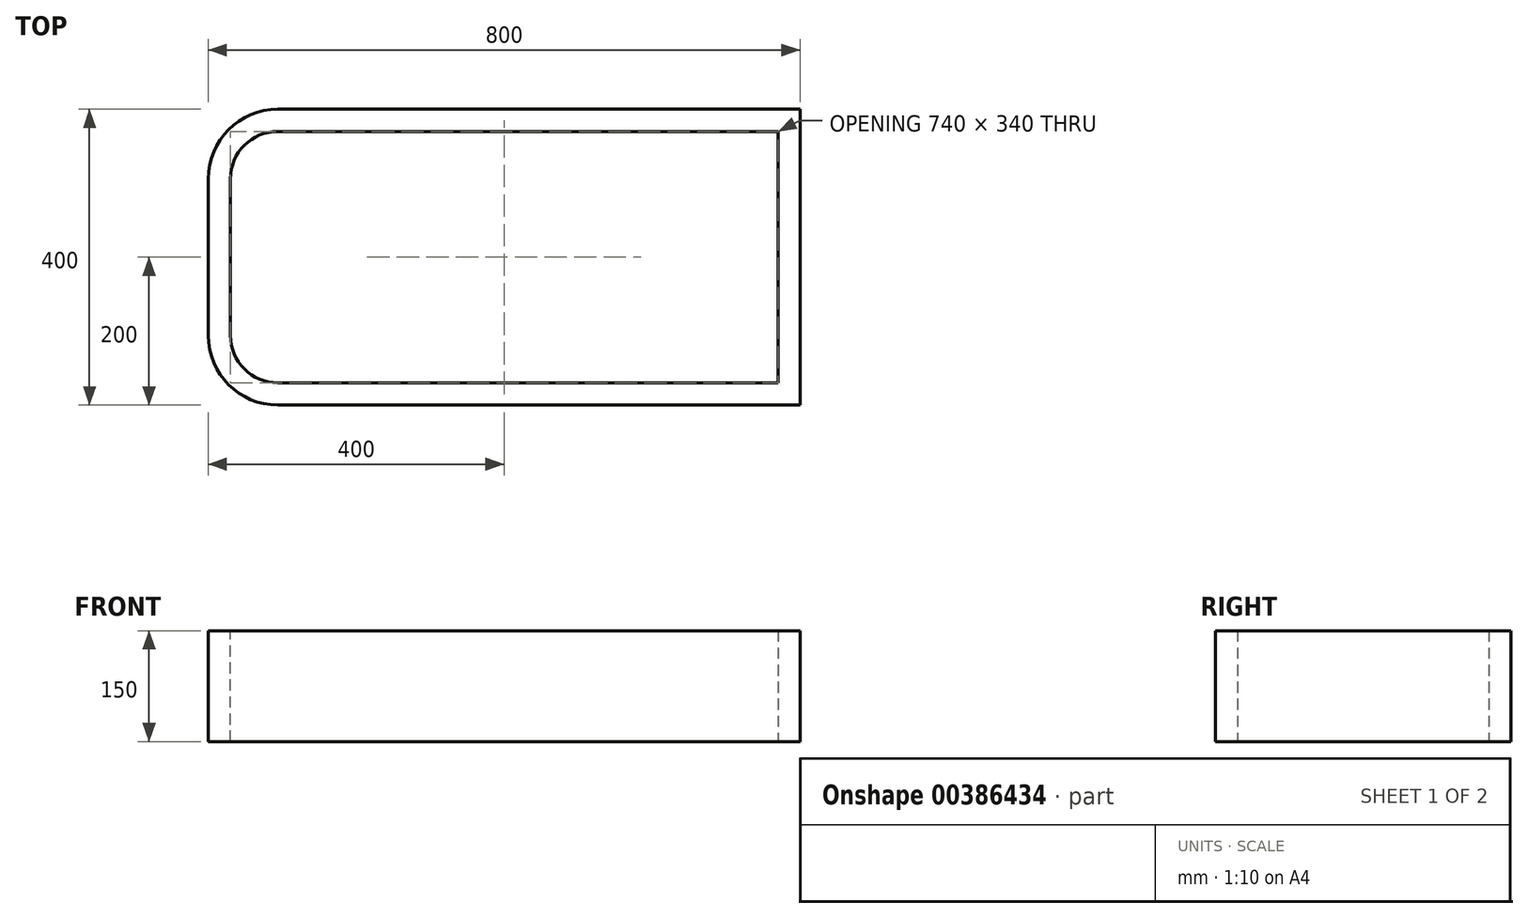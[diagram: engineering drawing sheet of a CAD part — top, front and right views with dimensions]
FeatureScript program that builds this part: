
annotation { "Feature Type Name" : "Feature", "Feature Type Description" : "" }
export const myFeature = defineFeature(function(context is Context, id is Id, definition is map)
    precondition{}
    {
        {
            var Q0;
            Q0=qCreatedBy(makeId("Top.planeOp"),FACE);
            var sketch = newSketch(context, id + "F0", { "sketchPlane" : qUnion([Q0])});
            skLineSegment(sketch, "E0.bottom", {"start": v(400, -200) * mm, "end": v(-400, -200) * mm});
            skLineSegment(sketch, "E0.top", {"start": v(400, 200) * mm, "end": v(-400, 200) * mm});
            skLineSegment(sketch, "E0.left", {"start": v(400, -200) * mm, "end": v(400, 200) * mm});
            skLineSegment(sketch, "E0.right", {"start": v(-400, -200) * mm, "end": v(-400, 200) * mm});
            skPoint(sketch, "E0.middle", {"position": v(0, 0) * mm});
            skSolve(sketch);
        }
        {
            var Q0;
            Q0=makeQuery(id+"F0.imprint","IMPRINT",FACE,{"disambiguationData":[TD([[makeQuery(id+"F0.imprint","IMPRINT",EDGE,{"derivedFrom":sQuery(id+"F0.wireOp",EDGE,"E0.bottom")}),-1.0]])]});
            extrude(context, id + "F1", {"entities" : qUnion([Q0]), "depth" : 150 * mm});
        }
        {
            var Q0;
            Q0=makeQuery(id+"F1.opExtrude","SWEPT_EDGE",EDGE,{"disambiguationData":[OSD([sQuery(id+"F0.wireOp",EDGE,"E0.top"),sQuery(id+"F0.wireOp",EDGE,"E0.right")])]});
            var Q1;
            Q1=makeQuery(id+"F1.opExtrude","SWEPT_EDGE",EDGE,{"disambiguationData":[OSD([sQuery(id+"F0.wireOp",EDGE,"E0.bottom"),sQuery(id+"F0.wireOp",EDGE,"E0.right")])]});
            fillet(context, id + "F2", {"entities" : qUnion([Q0, Q1]), "radius" : 94.15 * mm, "tangentPropagation" : true, "allowEdgeOverflow" : false});
        }
        {
            var Q0;
            Q0=makeQuery(id+"F1.opExtrude","CAP_FACE",FACE,{"disambiguationData":[OSD([sQuery(id+"F0.wireOp",EDGE,"E0.bottom"),sQuery(id+"F0.wireOp",EDGE,"E0.top"),sQuery(id+"F0.wireOp",EDGE,"E0.left"),sQuery(id+"F0.wireOp",EDGE,"E0.right")])],"isStart":false});
            shell(context, id + "F3", {"entities" : qUnion([Q0]), "thickness" : 30 * mm});
        }
        {
            var Q0;
            Q0=makeQuery(id+"F3.opShell","OFFSET_FACE",FACE,{"disambiguationData":[OSD([sQuery(id+"F0.wireOp",EDGE,"E0.bottom"),sQuery(id+"F0.wireOp",EDGE,"E0.top"),sQuery(id+"F0.wireOp",EDGE,"E0.left"),sQuery(id+"F0.wireOp",EDGE,"E0.right")])]});
            extrude(context, id + "F4", {"entities" : qUnion([Q0]), "operationType" : NewBodyOperationType.REMOVE, "oppositeDirection" : true, "depth" : 202 * mm, "offsetDistance" : 25 * mm});
        }
    });
